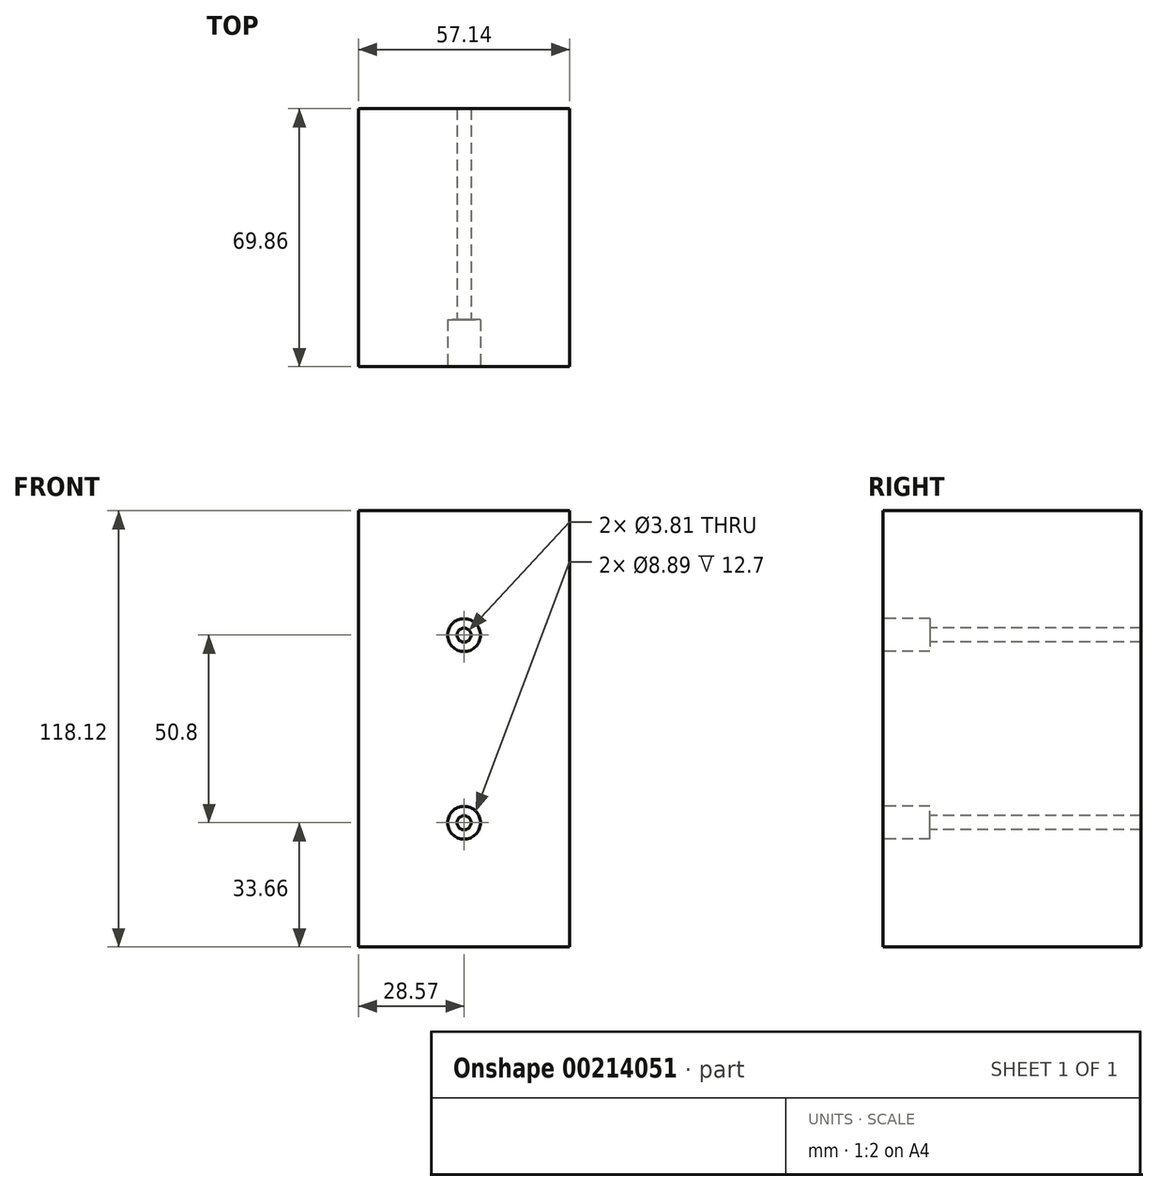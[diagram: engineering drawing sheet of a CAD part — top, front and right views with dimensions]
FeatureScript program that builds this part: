
annotation { "Feature Type Name" : "Feature", "Feature Type Description" : "" }
export const myFeature = defineFeature(function(context is Context, id is Id, definition is map)
    precondition{}
    {
        {
            var Q0;
            Q0=qCreatedBy(makeId("Top.planeOp"),FACE);
            cPlane(context, id + "F0", {"entities" : qUnion([Q0]), "cplaneType" : CPlaneType.OFFSET, "offset" : 25.4 * mm, "oppositeDirection" : true, "width" : 152.4 * mm, "height" : 152.4 * mm});
        }
        {
            var Q0;
            Q0=qCreatedBy(makeId("Front.planeOp"),FACE);
            var sketch = newSketch(context, id + "F1", { "sketchPlane" : qUnion([Q0])});
            skLineSegment(sketch, "E0.bottom", {"start": v(28.57, -59.06) * mm, "end": v(-28.58, -59.06) * mm});
            skLineSegment(sketch, "E0.top", {"start": v(28.58, 59.06) * mm, "end": v(-28.57, 59.06) * mm});
            skLineSegment(sketch, "E0.left", {"start": v(28.57, -59.06) * mm, "end": v(28.58, 59.06) * mm});
            skLineSegment(sketch, "E0.right", {"start": v(-28.58, -59.06) * mm, "end": v(-28.57, 59.05) * mm});
            skPoint(sketch, "E0.middle", {"position": v(0, 0) * mm});
            skSolve(sketch);
        }
        {
            var Q0;
            Q0=makeQuery(id+"F1.imprint","IMPRINT",FACE,{"disambiguationData":[TD([[makeQuery(id+"F1.imprint","IMPRINT",EDGE,{"derivedFrom":sQuery(id+"F1.wireOp",EDGE,"E0.bottom")}),-1.0]])]});
            extrude(context, id + "F2", {"entities" : qUnion([Q0]), "endBound" : BoundingType.SYMMETRIC, "depth" : 69.85 * mm});
        }
        {
            var Q0;
            Q0=makeQuery(id+"F2.opExtrude","CAP_FACE",FACE,{"disambiguationData":[OSD([sQuery(id+"F1.wireOp",EDGE,"E0.bottom"),sQuery(id+"F1.wireOp",EDGE,"E0.top"),sQuery(id+"F1.wireOp",EDGE,"E0.left"),sQuery(id+"F1.wireOp",EDGE,"E0.right")])],"isStart":false});
            var sketch = newSketch(context, id + "F3", { "sketchPlane" : qUnion([Q0])});
            skPoint(sketch, "E1", {"position": v(0, -25.4) * mm});
            skSolve(sketch);
        }
        {
            var Q0;
            Q0=sQuery(id+"F3.wireOp",VERTEX,"E1");
            var Q1;
            Q1=makeQuery(id+"F2.opExtrude","SWEPT_BODY",BODY,{"disambiguationData":[OSD([sQuery(id+"F1.wireOp",EDGE,"E0.bottom"),sQuery(id+"F1.wireOp",EDGE,"E0.top"),sQuery(id+"F1.wireOp",EDGE,"E0.left"),sQuery(id+"F1.wireOp",EDGE,"E0.right")])]});
            hole(context, id + "F4", {"style" : HoleStyle.C_BORE, "endStyle" : HoleEndStyle.THROUGH, "holeDiameter" : 3.8 * mm, "cBoreDiameter" : 8.9 * mm, "cBoreDepth" : 12.7 * mm, "locations" : qUnion([Q0]), "scope" : qUnion([Q1]), "isTappedThrough" : true});
        }
        {
            var Q0;
            Q0=makeQuery(id+"F2.opExtrude","SWEPT_BODY",BODY,{"disambiguationData":[OSD([sQuery(id+"F1.wireOp",EDGE,"E0.bottom"),sQuery(id+"F1.wireOp",EDGE,"E0.top"),sQuery(id+"F1.wireOp",EDGE,"E0.left"),sQuery(id+"F1.wireOp",EDGE,"E0.right")])]});
            var Q1;
            Q1=qCreatedBy(makeId("Top.planeOp"),FACE);
            mirror(context, id + "F5", {"operationType" : NewBodyOperationType.INTERSECT, "entities" : qUnion([Q0]), "mirrorPlane" : qUnion([Q1])});
        }
    });
